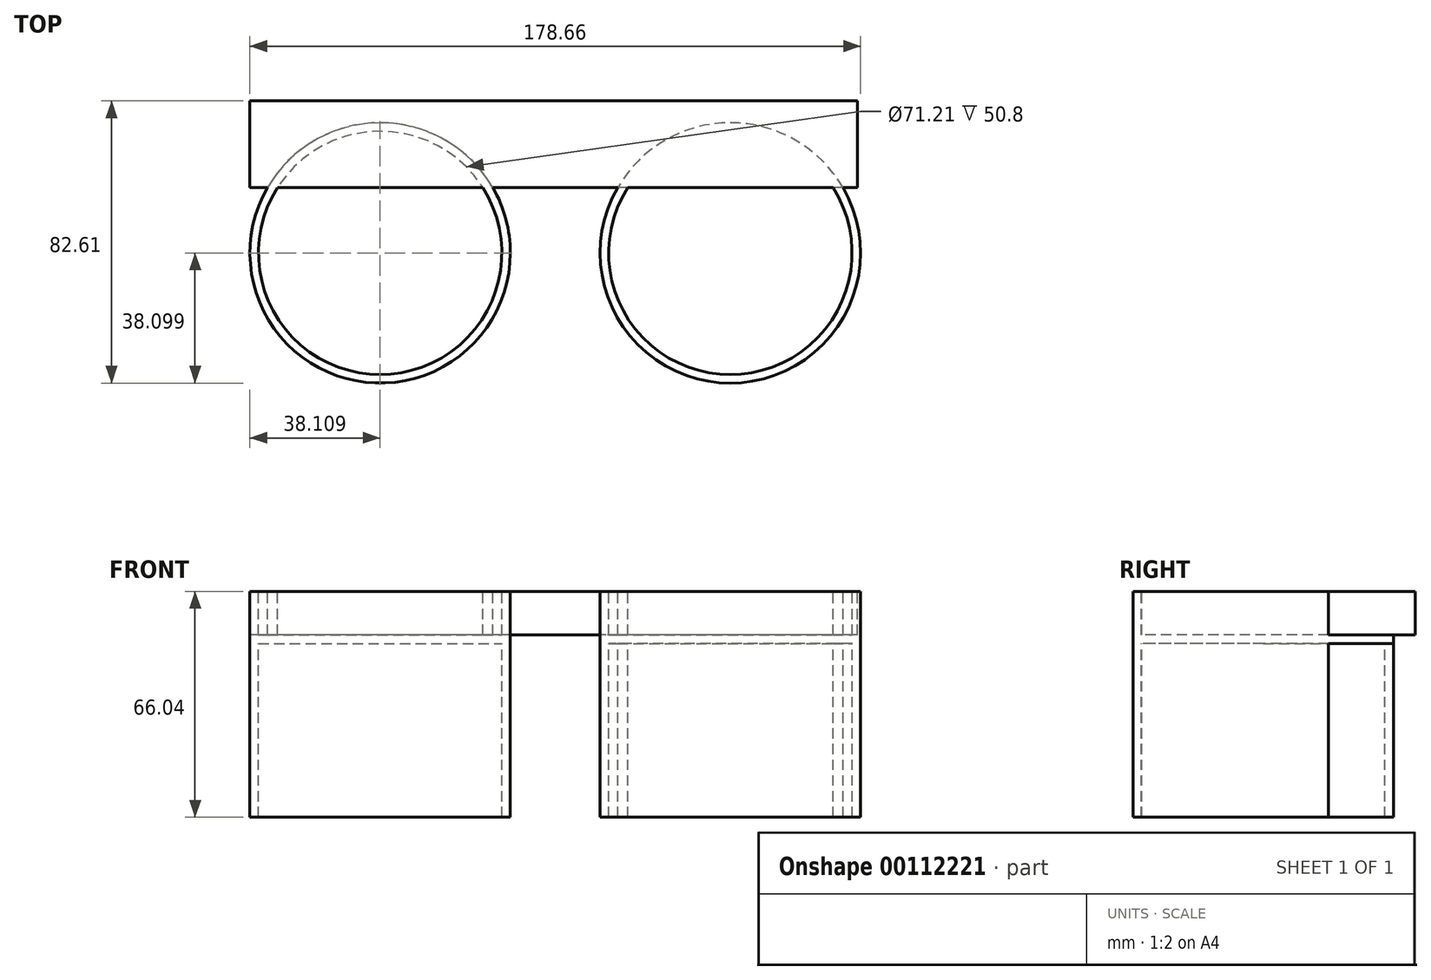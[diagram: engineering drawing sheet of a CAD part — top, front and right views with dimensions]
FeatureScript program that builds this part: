
annotation { "Feature Type Name" : "Feature", "Feature Type Description" : "" }
export const myFeature = defineFeature(function(context is Context, id is Id, definition is map)
    precondition{}
    {
        {
            var Q0;
            Q0=qCreatedBy(makeId("Front.planeOp"),FACE);
            var sketch = newSketch(context, id + "F0", { "sketchPlane" : qUnion([Q0])});
            skLineSegment(sketch, "E0.bottom", {"start": v(88.9, -6.35) * mm, "end": v(-88.9, -6.35) * mm});
            skLineSegment(sketch, "E0.top", {"start": v(88.9, 6.35) * mm, "end": v(-88.9, 6.35) * mm});
            skLineSegment(sketch, "E0.left", {"start": v(88.9, -6.35) * mm, "end": v(88.9, 6.35) * mm});
            skLineSegment(sketch, "E0.right", {"start": v(-88.9, -6.35) * mm, "end": v(-88.9, 6.35) * mm});
            skPoint(sketch, "E0.middle", {"position": v(0, 0) * mm});
            skSolve(sketch);
        }
        {
            var Q0;
            Q0 = qSketchRegion(id + "F0", true);
            extrude(context, id + "F1", {"entities" : qUnion([Q0]), "depth" : 25.4 * mm});
        }
        {
            var Q0;
            Q0=makeQuery(id+"F1.opExtrude","SWEPT_FACE",FACE,{"disambiguationData":[OSD([sQuery(id+"F0.wireOp",EDGE,"E0.top")])]});
            var sketch = newSketch(context, id + "F2", { "sketchPlane" : qUnion([Q0])});
            skCircle(sketch, "E1", {"center": v(-50.8, -44.51) * mm, "radius": 38.1 * mm});
            skCircle(sketch, "E2", {"center": v(-50.8, -44.51) * mm, "radius": 35.6 * mm});
            skCircle(sketch, "E3", {"center": v(51.66, -44.51) * mm, "radius": 38.1 * mm});
            skCircle(sketch, "E4", {"center": v(51.66, -44.51) * mm, "radius": 35.61 * mm});
            skSolve(sketch);
        }
        {
            var Q0;
            {var subQ0=sQuery(id+"F2.wireOp",EDGE,"E1");var subQ1=makeQuery(id+"F1.opExtrude","CAP_EDGE",EDGE,{"disambiguationData":[OSD([sQuery(id+"F0.wireOp",EDGE,"E0.top")])],"isStart":false});var subQ2=makeQuery(id+"F2.imprint","INTERSECT",VERTEX,{"disambiguationData":[OD(0.0)],"derivedFrom":[subQ1,subQ0]});Q0=makeQuery(id+"F2.imprint","IMPRINT",FACE,{"disambiguationData":[TD([[makeQuery(id+"F2.imprint","IMPRINT",EDGE,{"disambiguationData":[TD([[subQ2,1.0]])],"derivedFrom":subQ0}),1.0]])]});}
            var Q1;
            {var subQ0=sQuery(id+"F2.wireOp",EDGE,"E1");var subQ1=makeQuery(id+"F1.opExtrude","CAP_EDGE",EDGE,{"disambiguationData":[OSD([sQuery(id+"F0.wireOp",EDGE,"E0.top")])],"isStart":false});var subQ2=makeQuery(id+"F2.imprint","INTERSECT",VERTEX,{"disambiguationData":[OD(0.0)],"derivedFrom":[subQ1,subQ0]});Q1=makeQuery(id+"F2.imprint","IMPRINT",FACE,{"disambiguationData":[TD([[makeQuery(id+"F2.imprint","IMPRINT",EDGE,{"disambiguationData":[TD([[subQ2,-1.0]])],"derivedFrom":subQ0}),1.0]])]});}
            var Q2;
            {var subQ0=sQuery(id+"F2.wireOp",EDGE,"E3");var subQ1=makeQuery(id+"F1.opExtrude","CAP_EDGE",EDGE,{"disambiguationData":[OSD([sQuery(id+"F0.wireOp",EDGE,"E0.top")])],"isStart":false});var subQ2=makeQuery(id+"F2.imprint","INTERSECT",VERTEX,{"disambiguationData":[OD(0.0)],"derivedFrom":[subQ1,subQ0]});Q2=makeQuery(id+"F2.imprint","IMPRINT",FACE,{"disambiguationData":[TD([[makeQuery(id+"F2.imprint","IMPRINT",EDGE,{"disambiguationData":[TD([[subQ2,1.0]])],"derivedFrom":subQ0}),1.0]])]});}
            extrude(context, id + "F3", {"entities" : qUnion([Q0, Q1, Q2]), "oppositeDirection" : true, "depth" : 66.04 * mm});
        }
        {
            var Q0;
            Q0=makeQuery(id+"F3.boolean.opBoolean","MERGE",FACE,{"derivedFrom":[makeQuery(id+"F1.opExtrude","SWEPT_FACE",FACE,{"disambiguationData":[OSD([sQuery(id+"F0.wireOp",EDGE,"E0.bottom")])]}),makeQuery(id+"F3.opExtrude","CAP_FACE",FACE,{"disambiguationData":[OSD([sQuery(id+"F0.wireOp",EDGE,"E0.top"),sQuery(id+"F2.wireOp",EDGE,"E1"),sQuery(id+"F2.wireOp",EDGE,"E2")])],"isStart":false})]});
            var sketch = newSketch(context, id + "F4", { "sketchPlane" : qUnion([Q0])});
            skCircle(sketch, "E5", {"center": v(-50.8, 44.51) * mm, "radius": 38.1 * mm});
            skCircle(sketch, "E6", {"center": v(51.66, 44.51) * mm, "radius": 38.1 * mm});
            skSolve(sketch);
        }
        {
            var Q0;
            Q0 = qSketchRegion(id + "F4", true);
            extrude(context, id + "F5", {"entities" : qUnion([Q0]), "operationType" : NewBodyOperationType.ADD, "depth" : 2.54 * mm});
        }
    });
